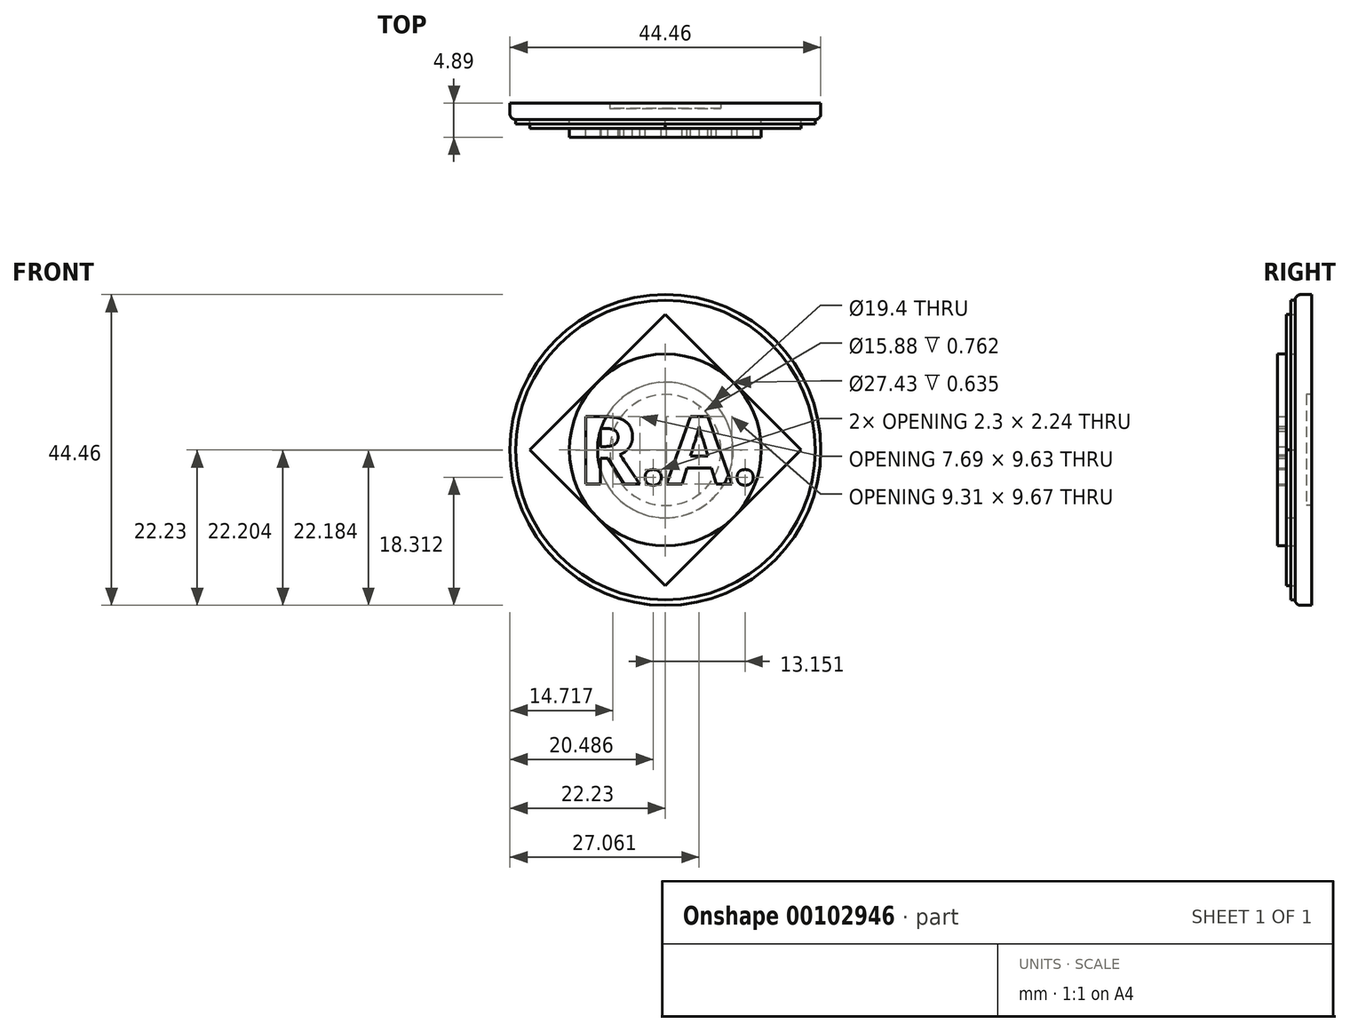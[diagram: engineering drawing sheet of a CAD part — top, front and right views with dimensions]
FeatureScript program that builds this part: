
annotation { "Feature Type Name" : "Feature", "Feature Type Description" : "" }
export const myFeature = defineFeature(function(context is Context, id is Id, definition is map)
    precondition{}
    {
        {
            var Q0;
            Q0=qCreatedBy(makeId("Front.planeOp"),FACE);
            var sketch = newSketch(context, id + "F0", { "sketchPlane" : qUnion([Q0])});
            skCircle(sketch, "E0", {"center": v(0, 0) * mm, "radius": 22.23 * mm});
            skSolve(sketch);
        }
        {
            var Q0;
            Q0=makeQuery(id+"F0.imprint","IMPRINT",FACE,{"disambiguationData":[TD([[makeQuery(id+"F0.imprint","IMPRINT",EDGE,{"derivedFrom":sQuery(id+"F0.wireOp",EDGE,"E0")}),1.0]])]});
            extrude(context, id + "F1", {"entities" : qUnion([Q0]), "depth" : 1.59 * mm});
        }
        {
            var Q0;
            Q0=makeQuery(id+"F1.opExtrude","CAP_EDGE",EDGE,{"disambiguationData":[OSD([sQuery(id+"F0.wireOp",EDGE,"E0")])],"isStart":false});
            fillet(context, id + "F2", {"entities" : qUnion([Q0]), "radius" : 0.8 * mm, "tangentPropagation" : true, "allowEdgeOverflow" : false});
        }
        {
            var Q0;
            Q0=makeQuery(id+"F1.opExtrude","CAP_FACE",FACE,{"disambiguationData":[OSD([sQuery(id+"F0.wireOp",EDGE,"E0")])],"isStart":true});
            var sketch = newSketch(context, id + "F3", { "sketchPlane" : qUnion([Q0])});
            skCircle(sketch, "E1", {"center": v(0, 0) * mm, "radius": 7.94 * mm});
            skSolve(sketch);
        }
        {
            var Q0;
            Q0=makeQuery(id+"F3.imprint","IMPRINT",FACE,{"disambiguationData":[TD([[makeQuery(id+"F3.imprint","IMPRINT",EDGE,{"derivedFrom":sQuery(id+"F3.wireOp",EDGE,"E1")}),-1.0]])]});
            extrude(context, id + "F4", {"entities" : qUnion([Q0]), "operationType" : NewBodyOperationType.ADD, "depth" : 0.76 * mm});
        }
        {
            var Q0;
            Q0=makeQuery(id+"F1.opExtrude","CAP_FACE",FACE,{"disambiguationData":[OSD([sQuery(id+"F0.wireOp",EDGE,"E0")])],"isStart":false});
            var sketch = newSketch(context, id + "F5", { "sketchPlane" : qUnion([Q0])});
            skLineSegment(sketch, "E2", {"start": v(0, 19.4) * mm, "end": v(19.4, 0) * mm});
            skLineSegment(sketch, "E3", {"start": v(19.4, 0) * mm, "end": v(0, -19.4) * mm});
            skLineSegment(sketch, "E4", {"start": v(0, -19.4) * mm, "end": v(-19.4, 0) * mm});
            skLineSegment(sketch, "E5", {"start": v(-19.4, 0) * mm, "end": v(0, 19.4) * mm});
            skCircle(sketch, "E6", {"center": v(0, 0) * mm, "radius": 13.72 * mm});
            skLineSegment(sketch, "E7.bottom", {"start": v(9.7, 9.7) * mm, "end": v(-9.7, 9.7) * mm});
            skLineSegment(sketch, "E7.top", {"start": v(9.7, -9.7) * mm, "end": v(-9.7, -9.7) * mm});
            skLineSegment(sketch, "E7.left", {"start": v(9.7, 9.7) * mm, "end": v(9.7, -9.7) * mm});
            skLineSegment(sketch, "E7.right", {"start": v(-9.7, 9.7) * mm, "end": v(-9.7, -9.7) * mm});
            skCircle(sketch, "E8", {"center": v(0, 0) * mm, "radius": 9.7 * mm});
            skLineSegment(sketch, "E9.bottom", {"start": v(6.86, -6.86) * mm, "end": v(-6.86, -6.86) * mm});
            skLineSegment(sketch, "E9.top", {"start": v(6.86, 6.86) * mm, "end": v(-6.86, 6.86) * mm});
            skLineSegment(sketch, "E9.left", {"start": v(6.86, -6.86) * mm, "end": v(6.86, 6.86) * mm});
            skLineSegment(sketch, "E9.right", {"start": v(-6.86, -6.86) * mm, "end": v(-6.86, 6.86) * mm});
            skText(sketch, "E10", { "text": "R.A.", "fontName": "OpenSans-BoldItalic.ttf"});
            const initialGuessF5  = {"E10": [-0.00586, -0.00247, 1, 0, 0.00494]};
            skSetInitialGuess(sketch, initialGuessF5);
            skSolve(sketch);
        }
        {
            var Q0;
            {var subQ0=sQuery(id+"F5.wireOp",EDGE,"E5");var subQ1=sQuery(id+"F5.wireOp",EDGE,"E4");var subQ2=makeQuery(id+"F5.imprint","INTERSECT",VERTEX,{"derivedFrom":[subQ1,subQ0]});Q0=makeQuery(id+"F5.imprint","IMPRINT",FACE,{"disambiguationData":[TD([[makeQuery(id+"F5.imprint","IMPRINT",EDGE,{"disambiguationData":[TD([[subQ2,1.0]])],"derivedFrom":subQ1}),-1.0]])]});}
            var Q1;
            {var subQ0=sQuery(id+"F5.wireOp",EDGE,"E5");var subQ1=sQuery(id+"F5.wireOp",EDGE,"E2");var subQ2=makeQuery(id+"F5.imprint","INTERSECT",VERTEX,{"derivedFrom":[subQ1,subQ0]});Q1=makeQuery(id+"F5.imprint","IMPRINT",FACE,{"disambiguationData":[TD([[makeQuery(id+"F5.imprint","IMPRINT",EDGE,{"disambiguationData":[TD([[subQ2,-1.0]])],"derivedFrom":subQ1}),-1.0]])]});}
            var Q2;
            {var subQ0=sQuery(id+"F5.wireOp",EDGE,"E3");var subQ1=sQuery(id+"F5.wireOp",EDGE,"E2");var subQ2=makeQuery(id+"F5.imprint","INTERSECT",VERTEX,{"derivedFrom":[subQ1,subQ0]});Q2=makeQuery(id+"F5.imprint","IMPRINT",FACE,{"disambiguationData":[TD([[makeQuery(id+"F5.imprint","IMPRINT",EDGE,{"disambiguationData":[TD([[subQ2,1.0]])],"derivedFrom":subQ1}),-1.0]])]});}
            var Q3;
            {var subQ17=sQuery(id+"F0.wireOp",EDGE,"E0");Q3=makeQuery(id+"F5.imprint","IMPRINT",FACE,{"disambiguationData":[TD([[makeQuery(id+"F5.imprint","IMPRINT",EDGE,{"derivedFrom":makeQuery(id+"F2.opFillet","BLEND_EDGE",EDGE,{"blendedFrom":[makeQuery(id+"F1.opExtrude","CAP_EDGE",EDGE,{"disambiguationData":[OSD([subQ17])],"isStart":false}),makeQuery(id+"F1.opExtrude","CAP_FACE",FACE,{"disambiguationData":[OSD([subQ17])],"isStart":false})],"blendedInto":[makeQuery(id+"F1.opExtrude","CAP_FACE",FACE,{"disambiguationData":[OSD([subQ17])],"isStart":false})]})}),1.0]])]});}
            var Q4;
            {var subQ0=sQuery(id+"F5.wireOp",EDGE,"E4");var subQ1=sQuery(id+"F5.wireOp",EDGE,"E3");var subQ2=makeQuery(id+"F5.imprint","INTERSECT",VERTEX,{"derivedFrom":[subQ1,subQ0]});Q4=makeQuery(id+"F5.imprint","IMPRINT",FACE,{"disambiguationData":[TD([[makeQuery(id+"F5.imprint","IMPRINT",EDGE,{"disambiguationData":[TD([[subQ2,1.0]])],"derivedFrom":subQ1}),-1.0]])]});}
            extrude(context, id + "F6", {"entities" : qUnion([Q0, Q1, Q2, Q3, Q4]), "operationType" : NewBodyOperationType.ADD, "depth" : 0.64 * mm});
        }
        {
            var Q0;
            Q0 = qSketchRegion(id + "F5", true);
            var Q1;
            Q1=makeQuery(id+"F1.opExtrude","CAP_FACE",FACE,{"disambiguationData":[OSD([sQuery(id+"F0.wireOp",EDGE,"E0")])],"isStart":false});
            extrude(context, id + "F7", {"entities" : qUnion([Q0, Q1]), "depth" : 1.27 * mm});
        }
        {
            var Q0;
            Q0=makeQuery(id+"F7.boolean.opBoolean","MERGE",FACE,{"derivedFrom":[makeQuery(id+"F7.opExtrude","CAP_FACE",FACE,{"disambiguationData":[OSD([sQuery(id+"F5.wireOp",EDGE,"E2"),sQuery(id+"F5.wireOp",EDGE,"E3"),sQuery(id+"F5.wireOp",EDGE,"E4"),sQuery(id+"F5.wireOp",EDGE,"E5"),sQuery(id+"F5.wireOp",EDGE,"E8")])],"isStart":false}),makeQuery(id+"F7.opExtrude","CAP_FACE",FACE,{"disambiguationData":[OSD([sQuery(id+"F0.wireOp",EDGE,"E0")])],"isStart":false})]});
            var sketch = newSketch(context, id + "F8", { "sketchPlane" : qUnion([Q0])});
            skCircle(sketch, "E11", {"center": v(0, 0) * mm, "radius": 13.72 * mm});
            skText(sketch, "E12", { "text": "R.A.", "fontName": "OpenSans-Bold.ttf"});
            const initialGuessF8  = {"E12": [-0.01257, -0.00486, 1, 0, 0.00971]};
            skSetInitialGuess(sketch, initialGuessF8);
            skSolve(sketch);
        }
        {
            var Q0;
            Q0=makeQuery(id+"F8.imprint","IMPRINT",FACE,{"disambiguationData":[TD([[makeQuery(id+"F8.imprint","IMPRINT",EDGE,{"derivedFrom":sQuery(id+"F8.wireOp",EDGE,"E12.sketch_text.stroke-7")}),1.0]])]});
            var Q1;
            Q1=makeQuery(id+"F8.imprint","IMPRINT",FACE,{"disambiguationData":[TD([[makeQuery(id+"F8.imprint","IMPRINT",EDGE,{"derivedFrom":sQuery(id+"F8.wireOp",EDGE,"E12.sketch_text.stroke-0")}),1.0]])]});
            var Q2;
            Q2=makeQuery(id+"F8.imprint","IMPRINT",FACE,{"disambiguationData":[TD([[makeQuery(id+"F8.imprint","IMPRINT",EDGE,{"derivedFrom":sQuery(id+"F8.wireOp",EDGE,"E12.sketch_text.stroke-35")}),1.0]])]});
            var Q3;
            {var subQ5=sQuery(id+"F8.wireOp",EDGE,"E12.sketch_text.stroke-12");Q3=makeQuery(id+"F8.imprint","IMPRINT",FACE,{"disambiguationData":[TD([[makeQuery(id+"F8.imprint","IMPRINT",EDGE,{"derivedFrom":subQ5}),1.0]])]});}
            extrude(context, id + "F9", {"entities" : qUnion([Q0, Q1, Q2, Q3]), "depth" : 1.27 * mm});
        }
    });
